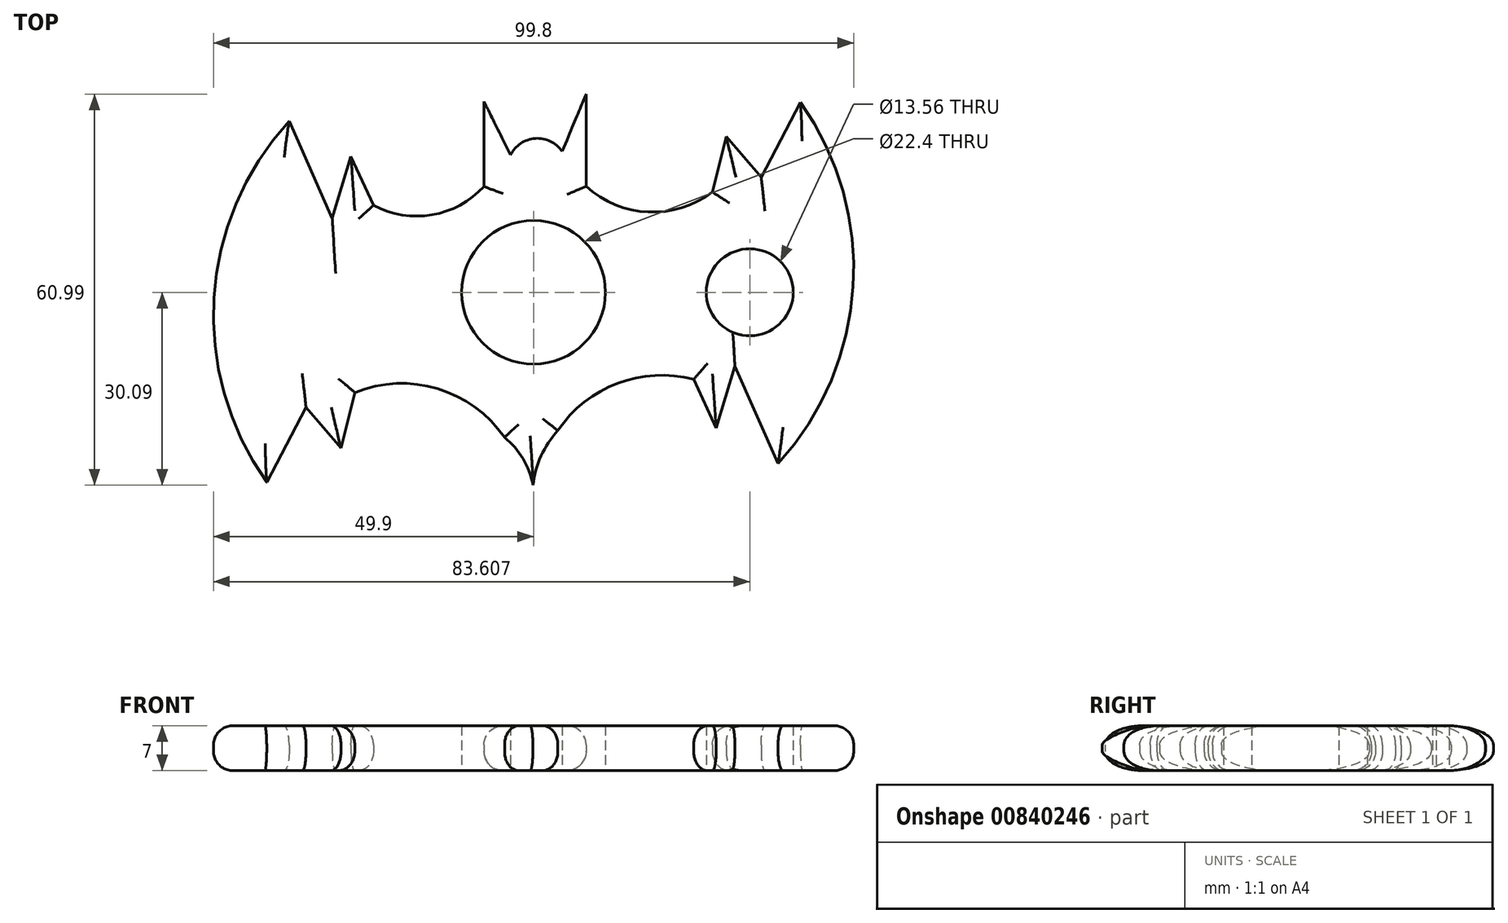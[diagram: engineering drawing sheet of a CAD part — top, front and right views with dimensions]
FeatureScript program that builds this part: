
annotation { "Feature Type Name" : "Feature", "Feature Type Description" : "" }
export const myFeature = defineFeature(function(context is Context, id is Id, definition is map)
    precondition{}
    {
        {
            var Q0;
            Q0=qCreatedBy(makeId("Top.planeOp"),FACE);
            var sketch = newSketch(context, id + "F0", { "sketchPlane" : qUnion([Q0])});
            skCircle(sketch, "E0", {"center": v(0, 0) * mm, "radius": 11.2 * mm});
            skCircle(sketch, "E1", {"center": v(0, 0) * mm, "radius": 13.2 * mm});
            skArc(sketch, "E2", {"start": v(-38.1, 26.72) * mm, "mid": v(-49.82, -0.84) * mm, "end": v(-41.61, -29.64) * mm});
            skArc(sketch, "E3.1.0", {"start": v(38.1, -26.72) * mm, "mid": v(49.82, 0.84) * mm, "end": v(41.61, 29.64) * mm});
            skLineSegment(sketch, "E4", {"start": v(-41.61, -29.64) * mm, "end": v(-35.48, -17.96) * mm});
            skLineSegment(sketch, "E5", {"start": v(-35.48, -17.96) * mm, "end": v(-35.48, -24.97) * mm});
            skArc(sketch, "E6", {"start": v(-4.53, -22.63) * mm, "mid": v(-14.98, -15.03) * mm, "end": v(-27.89, -15.62) * mm});
            skLineSegment(sketch, "E7.1.0", {"start": v(41.61, 29.64) * mm, "end": v(35.48, 17.96) * mm});
            skLineSegment(sketch, "E7.1.1", {"start": v(35.48, 17.96) * mm, "end": v(30.03, 24.29) * mm});
            skLineSegment(sketch, "E7.1.2", {"start": v(30.03, 24.29) * mm, "end": v(27.89, 15.62) * mm});
            skLineSegment(sketch, "E8", {"start": v(38.1, -26.72) * mm, "end": v(31.4, -11.53) * mm});
            skLineSegment(sketch, "E9", {"start": v(31.4, -11.53) * mm, "end": v(28.47, -21.17) * mm});
            skLineSegment(sketch, "E10", {"start": v(28.47, -21.17) * mm, "end": v(24.97, -13.58) * mm});
            skArc(sketch, "E11.1.0", {"start": v(-24.97, 13.58) * mm, "mid": v(-15.85, 12.08) * mm, "end": v(-7.74, 16.5) * mm});
            skLineSegment(sketch, "E11.1.2", {"start": v(-28.47, 21.17) * mm, "end": v(-24.97, 13.58) * mm});
            skLineSegment(sketch, "E11.1.4", {"start": v(-31.4, 11.53) * mm, "end": v(-28.47, 21.17) * mm});
            skLineSegment(sketch, "E11.1.5", {"start": v(-38.1, 26.72) * mm, "end": v(-31.4, 11.53) * mm});
            skArc(sketch, "E12", {"start": v(0, -34.06) * mm, "mid": v(-0.76, -27.75) * mm, "end": v(-4.53, -22.63) * mm});
            skArc(sketch, "E13.1.0", {"start": v(8.2, 16.53) * mm, "mid": v(17.88, 12.52) * mm, "end": v(27.89, 15.62) * mm});
            skLineSegment(sketch, "E14", {"start": v(-7.74, 16.5) * mm, "end": v(-7.74, 29.75) * mm});
            skLineSegment(sketch, "E15", {"start": v(-7.74, 29.75) * mm, "end": v(-3.6, 21.41) * mm});
            skLineSegment(sketch, "E16", {"start": v(8.2, 16.53) * mm, "end": v(8.2, 30.9) * mm});
            skLineSegment(sketch, "E17", {"start": v(8.2, 30.9) * mm, "end": v(4.45, 21.97) * mm});
            skArc(sketch, "E18", {"start": v(4.45, 21.97) * mm, "mid": v(0.27, 24) * mm, "end": v(-3.6, 21.41) * mm});
            skArc(sketch, "E19", {"start": v(24.97, -13.58) * mm, "mid": v(13.1, -14.2) * mm, "end": v(3.78, -21.57) * mm});
            skArc(sketch, "E20", {"start": v(3.78, -21.57) * mm, "mid": v(0.47, -27.38) * mm, "end": v(0, -34.06) * mm});
            skLineSegment(sketch, "E21.1.0", {"start": v(-35.48, -17.96) * mm, "end": v(-30.03, -24.29) * mm});
            skLineSegment(sketch, "E21.1.1", {"start": v(-30.03, -24.29) * mm, "end": v(-27.89, -15.62) * mm});
            skCircle(sketch, "E22", {"center": v(33.7, 0) * mm, "radius": 6.78 * mm});
            skSolve(sketch);
        }
        {
            var Q0;
            Q0=makeQuery(id+"F0.imprint","IMPRINT",FACE,{"disambiguationData":[TD([[makeQuery(id+"F0.imprint","IMPRINT",EDGE,{"derivedFrom":sQuery(id+"F0.wireOp",EDGE,"E0")}),-1.0]])]});
            var Q1;
            Q1=makeQuery(id+"F0.imprint","IMPRINT",FACE,{"disambiguationData":[TD([[makeQuery(id+"F0.imprint","IMPRINT",EDGE,{"derivedFrom":sQuery(id+"F0.wireOp",EDGE,"E1")}),-1.0]])]});
            extrude(context, id + "F1", {"entities" : qUnion([Q0, Q1]), "depth" : 7 * mm, "offsetDistance" : 25 * mm});
        }
        {
            var Q0;
            Q0=makeQuery(id+"F1.opExtrude","CAP_EDGE",EDGE,{"disambiguationData":[OSD([sQuery(id+"F0.wireOp",EDGE,"E20")])],"isStart":false});
            var Q1;
            Q1=makeQuery(id+"F1.opExtrude","CAP_EDGE",EDGE,{"disambiguationData":[OSD([sQuery(id+"F0.wireOp",EDGE,"E19")])],"isStart":false});
            var Q2;
            Q2=makeQuery(id+"F1.opExtrude","CAP_EDGE",EDGE,{"disambiguationData":[OSD([sQuery(id+"F0.wireOp",EDGE,"E9")])],"isStart":false});
            var Q3;
            Q3=makeQuery(id+"F1.opExtrude","CAP_EDGE",EDGE,{"disambiguationData":[OSD([sQuery(id+"F0.wireOp",EDGE,"E3.1.0")])],"isStart":false});
            var Q4;
            Q4=makeQuery(id+"F1.opExtrude","CAP_EDGE",EDGE,{"disambiguationData":[OSD([sQuery(id+"F0.wireOp",EDGE,"E8")])],"isStart":false});
            var Q5;
            Q5=makeQuery(id+"F1.opExtrude","CAP_EDGE",EDGE,{"disambiguationData":[OSD([sQuery(id+"F0.wireOp",EDGE,"E7.1.0")])],"isStart":false});
            var Q6;
            Q6=makeQuery(id+"F1.opExtrude","CAP_EDGE",EDGE,{"disambiguationData":[OSD([sQuery(id+"F0.wireOp",EDGE,"E7.1.1")])],"isStart":false});
            var Q7;
            Q7=makeQuery(id+"F1.opExtrude","CAP_EDGE",EDGE,{"disambiguationData":[OSD([sQuery(id+"F0.wireOp",EDGE,"E7.1.2")])],"isStart":false});
            var Q8;
            Q8=makeQuery(id+"F1.opExtrude","CAP_EDGE",EDGE,{"disambiguationData":[OSD([sQuery(id+"F0.wireOp",EDGE,"E13.1.0")])],"isStart":false});
            var Q9;
            Q9=makeQuery(id+"F1.opExtrude","CAP_EDGE",EDGE,{"disambiguationData":[OSD([sQuery(id+"F0.wireOp",EDGE,"E16")])],"isStart":false});
            var Q10;
            Q10=makeQuery(id+"F1.opExtrude","CAP_EDGE",EDGE,{"disambiguationData":[OSD([sQuery(id+"F0.wireOp",EDGE,"E14")])],"isStart":false});
            var Q11;
            Q11=makeQuery(id+"F1.opExtrude","CAP_EDGE",EDGE,{"disambiguationData":[OSD([sQuery(id+"F0.wireOp",EDGE,"E11.1.0")])],"isStart":false});
            var Q12;
            Q12=makeQuery(id+"F1.opExtrude","CAP_EDGE",EDGE,{"disambiguationData":[OSD([sQuery(id+"F0.wireOp",EDGE,"E11.1.2")])],"isStart":false});
            var Q13;
            Q13=makeQuery(id+"F1.opExtrude","CAP_EDGE",EDGE,{"disambiguationData":[OSD([sQuery(id+"F0.wireOp",EDGE,"E11.1.5")])],"isStart":false});
            var Q14;
            Q14=makeQuery(id+"F1.opExtrude","CAP_EDGE",EDGE,{"disambiguationData":[OSD([sQuery(id+"F0.wireOp",EDGE,"E11.1.4")])],"isStart":false});
            var Q15;
            Q15=makeQuery(id+"F1.opExtrude","CAP_EDGE",EDGE,{"disambiguationData":[OSD([sQuery(id+"F0.wireOp",EDGE,"E2")])],"isStart":false});
            var Q16;
            Q16=makeQuery(id+"F1.opExtrude","CAP_EDGE",EDGE,{"disambiguationData":[OSD([sQuery(id+"F0.wireOp",EDGE,"E4")])],"isStart":false});
            var Q17;
            Q17=makeQuery(id+"F1.opExtrude","CAP_EDGE",EDGE,{"disambiguationData":[OSD([sQuery(id+"F0.wireOp",EDGE,"wEF84jsq-XExs-cQrN-D3yr-Ib7uIkRzdJAm")])],"isStart":false});
            var Q18;
            Q18=makeQuery(id+"F1.opExtrude","CAP_EDGE",EDGE,{"disambiguationData":[OSD([sQuery(id+"F0.wireOp",EDGE,"E12")])],"isStart":false});
            var Q19;
            Q19=makeQuery(id+"F1.opExtrude","CAP_EDGE",EDGE,{"disambiguationData":[OSD([sQuery(id+"F0.wireOp",EDGE,"E5")])],"isStart":false});
            var Q20;
            Q20=makeQuery(id+"F1.opExtrude","CAP_EDGE",EDGE,{"disambiguationData":[OSD([sQuery(id+"F0.wireOp",EDGE,"E10")])],"isStart":false});
            var Q21;
            Q21=makeQuery(id+"F1.opExtrude","CAP_EDGE",EDGE,{"disambiguationData":[OSD([sQuery(id+"F0.wireOp",EDGE,"E21.1.1")])],"isStart":false});
            var Q22;
            Q22=makeQuery(id+"F1.opExtrude","CAP_EDGE",EDGE,{"disambiguationData":[OSD([sQuery(id+"F0.wireOp",EDGE,"E6")])],"isStart":false});
            var Q23;
            Q23=makeQuery(id+"F1.opExtrude","CAP_EDGE",EDGE,{"disambiguationData":[OSD([sQuery(id+"F0.wireOp",EDGE,"E21.1.0")])],"isStart":false});
            var Q24;
            Q24=makeQuery(id+"F1.opExtrude","CAP_EDGE",EDGE,{"disambiguationData":[OSD([sQuery(id+"F0.wireOp",EDGE,"E3.1.0")])],"isStart":true});
            var Q25;
            Q25=makeQuery(id+"F1.opExtrude","CAP_EDGE",EDGE,{"disambiguationData":[OSD([sQuery(id+"F0.wireOp",EDGE,"E8")])],"isStart":true});
            var Q26;
            Q26=makeQuery(id+"F1.opExtrude","CAP_EDGE",EDGE,{"disambiguationData":[OSD([sQuery(id+"F0.wireOp",EDGE,"E9")])],"isStart":true});
            var Q27;
            Q27=makeQuery(id+"F1.opExtrude","CAP_EDGE",EDGE,{"disambiguationData":[OSD([sQuery(id+"F0.wireOp",EDGE,"E10")])],"isStart":true});
            var Q28;
            Q28=makeQuery(id+"F1.opExtrude","CAP_EDGE",EDGE,{"disambiguationData":[OSD([sQuery(id+"F0.wireOp",EDGE,"E19")])],"isStart":true});
            var Q29;
            Q29=makeQuery(id+"F1.opExtrude","CAP_EDGE",EDGE,{"disambiguationData":[OSD([sQuery(id+"F0.wireOp",EDGE,"E6")])],"isStart":true});
            var Q30;
            Q30=makeQuery(id+"F1.opExtrude","CAP_EDGE",EDGE,{"disambiguationData":[OSD([sQuery(id+"F0.wireOp",EDGE,"E12")])],"isStart":true});
            var Q31;
            Q31=makeQuery(id+"F1.opExtrude","CAP_EDGE",EDGE,{"disambiguationData":[OSD([sQuery(id+"F0.wireOp",EDGE,"E20")])],"isStart":true});
            var Q32;
            Q32=makeQuery(id+"F1.opExtrude","CAP_EDGE",EDGE,{"disambiguationData":[OSD([sQuery(id+"F0.wireOp",EDGE,"E21.1.1")])],"isStart":true});
            var Q33;
            Q33=makeQuery(id+"F1.opExtrude","CAP_EDGE",EDGE,{"disambiguationData":[OSD([sQuery(id+"F0.wireOp",EDGE,"E21.1.0")])],"isStart":true});
            var Q34;
            Q34=makeQuery(id+"F1.opExtrude","CAP_EDGE",EDGE,{"disambiguationData":[OSD([sQuery(id+"F0.wireOp",EDGE,"E4")])],"isStart":true});
            var Q35;
            Q35=makeQuery(id+"F1.opExtrude","CAP_EDGE",EDGE,{"disambiguationData":[OSD([sQuery(id+"F0.wireOp",EDGE,"E2")])],"isStart":true});
            var Q36;
            Q36=makeQuery(id+"F1.opExtrude","CAP_EDGE",EDGE,{"disambiguationData":[OSD([sQuery(id+"F0.wireOp",EDGE,"E11.1.5")])],"isStart":true});
            var Q37;
            Q37=makeQuery(id+"F1.opExtrude","CAP_EDGE",EDGE,{"disambiguationData":[OSD([sQuery(id+"F0.wireOp",EDGE,"E11.1.4")])],"isStart":true});
            var Q38;
            Q38=makeQuery(id+"F1.opExtrude","CAP_EDGE",EDGE,{"disambiguationData":[OSD([sQuery(id+"F0.wireOp",EDGE,"E14")])],"isStart":true});
            var Q39;
            Q39=makeQuery(id+"F1.opExtrude","CAP_EDGE",EDGE,{"disambiguationData":[OSD([sQuery(id+"F0.wireOp",EDGE,"E16")])],"isStart":true});
            var Q40;
            Q40=makeQuery(id+"F1.opExtrude","CAP_EDGE",EDGE,{"disambiguationData":[OSD([sQuery(id+"F0.wireOp",EDGE,"E13.1.0")])],"isStart":true});
            var Q41;
            Q41=makeQuery(id+"F1.opExtrude","CAP_EDGE",EDGE,{"disambiguationData":[OSD([sQuery(id+"F0.wireOp",EDGE,"E7.1.2")])],"isStart":true});
            var Q42;
            Q42=makeQuery(id+"F1.opExtrude","CAP_EDGE",EDGE,{"disambiguationData":[OSD([sQuery(id+"F0.wireOp",EDGE,"E7.1.1")])],"isStart":true});
            var Q43;
            Q43=makeQuery(id+"F1.opExtrude","CAP_EDGE",EDGE,{"disambiguationData":[OSD([sQuery(id+"F0.wireOp",EDGE,"E7.1.0")])],"isStart":true});
            var Q44;
            Q44=makeQuery(id+"F1.opExtrude","CAP_EDGE",EDGE,{"disambiguationData":[OSD([sQuery(id+"F0.wireOp",EDGE,"E11.1.0")])],"isStart":true});
            var Q45;
            Q45=makeQuery(id+"F1.opExtrude","CAP_EDGE",EDGE,{"disambiguationData":[OSD([sQuery(id+"F0.wireOp",EDGE,"E11.1.2")])],"isStart":true});
            fillet(context, id + "F2", {"entities" : qUnion([Q0, Q1, Q2, Q3, Q4, Q5, Q6, Q7, Q8, Q9, Q10, Q11, Q12, Q13, Q14, Q15, Q16, Q17, Q18, Q19, Q20, Q21, Q22, Q23, Q24, Q25, Q26, Q27, Q28, Q29, Q30, Q31, Q32, Q33, Q34, Q35, Q36, Q37, Q38, Q39, Q40, Q41, Q42, Q43, Q44, Q45]), "radius" : 3 * mm, "tangentPropagation" : true, "allowEdgeOverflow" : false});
        }
    });
